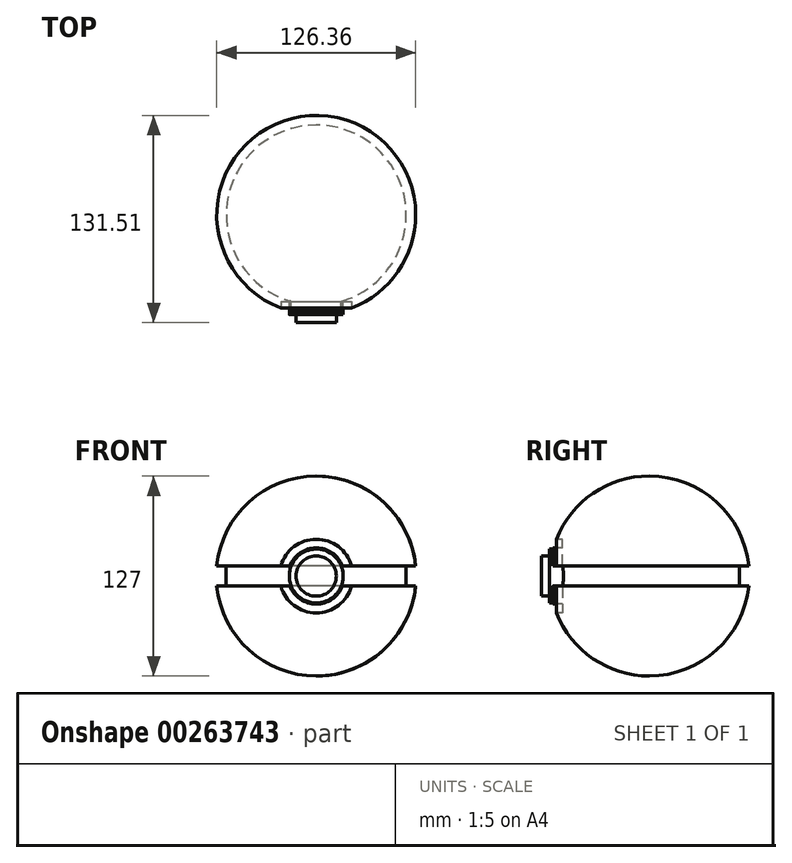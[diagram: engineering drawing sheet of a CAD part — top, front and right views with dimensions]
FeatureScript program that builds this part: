
annotation { "Feature Type Name" : "Feature", "Feature Type Description" : "" }
export const myFeature = defineFeature(function(context is Context, id is Id, definition is map)
    precondition{}
    {
        {
            var Q0;
            Q0=qCreatedBy(makeId("Front.planeOp"),FACE);
            var sketch = newSketch(context, id + "F0", { "sketchPlane" : qUnion([Q0])});
            skArc(sketch, "E0", {"start": v(0, -63.5) * mm, "mid": v(42.6, -47.1) * mm, "end": v(63.18, -6.35) * mm});
            skLineSegment(sketch, "E1", {"start": v(0, 63.5) * mm, "end": v(0, -63.5) * mm});
            skLineSegment(sketch, "E2", {"start": v(63.5, 0) * mm, "end": v(57.15, 0) * mm, "construction": true});
            skLineSegment(sketch, "E3", {"start": v(57.15, 0) * mm, "end": v(57.15, 6.35) * mm});
            skLineSegment(sketch, "E4", {"start": v(57.15, 6.35) * mm, "end": v(63.5, 6.35) * mm});
            skLineSegment(sketch, "E5.MirrorCS", {"start": v(57.15, -6.35) * mm, "end": v(63.5, -6.35) * mm});
            skLineSegment(sketch, "E6.MirrorCS", {"start": v(57.15, 0) * mm, "end": v(57.15, -6.35) * mm});
            skArc(sketch, "E7.trimOffspring", {"start": v(63.18, 6.35) * mm, "mid": v(42.6, 47.1) * mm, "end": v(0, 63.5) * mm});
            skSolve(sketch);
        }
        {
            var Q0;
            {var subQ3=sQuery(id+"F0.wireOp",EDGE,"E0");Q0=makeQuery(id+"F0.imprint","IMPRINT",FACE,{"disambiguationData":[TD([[makeQuery(id+"F0.imprint","IMPRINT",EDGE,{"derivedFrom":subQ3}),1.0]])]});}
            var Q1;
            Q1=sQuery(id+"F0.wireOp",EDGE,"E1");
            revolve(context, id + "F1", {"entities" : qUnion([Q0]), "axis" : qUnion([Q1]), "revolveType" : RevolveType.FULL});
        }
        {
            var Q0;
            Q0=qCreatedBy(makeId("Front.planeOp"),FACE);
            var sketch = newSketch(context, id + "F2", { "sketchPlane" : qUnion([Q0])});
            skCircle(sketch, "E8", {"center": v(0, 0) * mm, "radius": 17.1 * mm});
            skSolve(sketch);
        }
        {
            var Q0;
            Q0 = qSketchRegion(id + "F2", true);
            extrude(context, id + "F3", {"entities" : qUnion([Q0]), "operationType" : NewBodyOperationType.ADD, "depth" : 63.25 * mm});
        }
        {
            var Q0;
            Q0=makeQuery(id+"F3.opExtrude","CAP_FACE",FACE,{"disambiguationData":[OSD([sQuery(id+"F2.wireOp",EDGE,"E8")])],"isStart":false});
            var sketch = newSketch(context, id + "F4", { "sketchPlane" : qUnion([Q0])});
            skCircle(sketch, "E9", {"center": v(0, 0) * mm, "radius": 12.78 * mm});
            skSolve(sketch);
        }
        {
            var Q0;
            Q0 = qSketchRegion(id + "F4", true);
            extrude(context, id + "F5", {"entities" : qUnion([Q0]), "operationType" : NewBodyOperationType.ADD, "depth" : 5.08 * mm});
        }
        {
            var Q0;
            Q0=makeQuery(id+"F5.opExtrude","CAP_FACE",FACE,{"disambiguationData":[OSD([sQuery(id+"F4.wireOp",EDGE,"E9")])],"isStart":false});
            var sketch = newSketch(context, id + "F6", { "sketchPlane" : qUnion([Q0])});
            skCircle(sketch, "E10", {"center": v(0, 0) * mm, "radius": 17.86 * mm});
            skCircle(sketch, "E11", {"center": v(0, 0) * mm, "radius": 23.37 * mm});
            skSolve(sketch);
        }
        {
            var Q0;
            Q0 = qSketchRegion(id + "F6", true);
            extrude(context, id + "F7", {"entities" : qUnion([Q0]), "operationType" : NewBodyOperationType.REMOVE, "oppositeDirection" : true, "depth" : 13.2 * mm});
        }
    });
